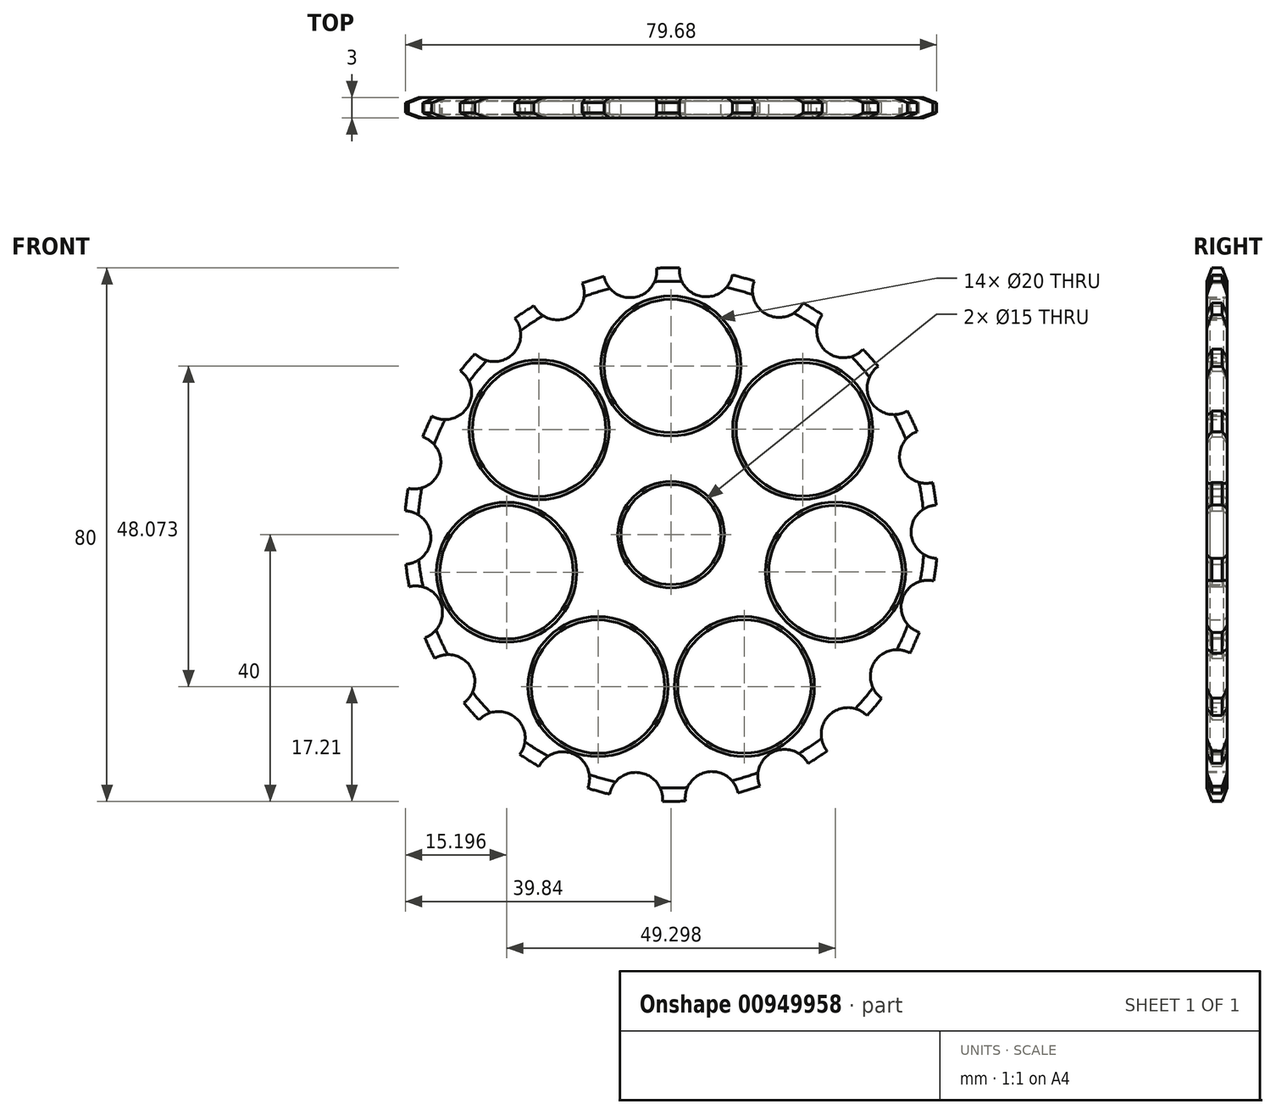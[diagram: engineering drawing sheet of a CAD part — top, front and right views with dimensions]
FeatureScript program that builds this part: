
annotation { "Feature Type Name" : "Feature", "Feature Type Description" : "" }
export const myFeature = defineFeature(function(context is Context, id is Id, definition is map)
    precondition{}
    {
        {
            var Q0;
            Q0=qCreatedBy(makeId("Front.planeOp"),FACE);
            var sketch = newSketch(context, id + "F0", { "sketchPlane" : qUnion([Q0])});
            skCircle(sketch, "E0", {"center": v(0, 0) * mm, "radius": 40 * mm});
            skCircle(sketch, "E1", {"center": v(-33.89, 21.25) * mm, "radius": 4 * mm});
            skCircle(sketch, "E2.1.0", {"center": v(-38.5, 10.85) * mm, "radius": 4 * mm});
            skCircle(sketch, "E2.2.0", {"center": v(-40, -0.44) * mm, "radius": 4 * mm});
            skCircle(sketch, "E2.3.0", {"center": v(-38.25, -11.7) * mm, "radius": 4 * mm});
            skCircle(sketch, "E2.4.0", {"center": v(-33.41, -22) * mm, "radius": 4 * mm});
            skCircle(sketch, "E2.5.0", {"center": v(-25.86, -30.52) * mm, "radius": 4 * mm});
            skCircle(sketch, "E2.6.0", {"center": v(-16.22, -36.57) * mm, "radius": 4 * mm});
            skCircle(sketch, "E2.7.0", {"center": v(-5.26, -39.65) * mm, "radius": 4 * mm});
            skCircle(sketch, "E2.8.0", {"center": v(6.13, -39.53) * mm, "radius": 4 * mm});
            skCircle(sketch, "E2.9.0", {"center": v(17.02, -36.2) * mm, "radius": 4 * mm});
            skCircle(sketch, "E2.10.0", {"center": v(26.53, -29.94) * mm, "radius": 4 * mm});
            skCircle(sketch, "E2.11.0", {"center": v(33.89, -21.25) * mm, "radius": 4 * mm});
            skCircle(sketch, "E2.12.0", {"center": v(38.5, -10.85) * mm, "radius": 4 * mm});
            skCircle(sketch, "E2.13.0", {"center": v(40, 0.44) * mm, "radius": 4 * mm});
            skCircle(sketch, "E2.14.0", {"center": v(38.25, 11.7) * mm, "radius": 4 * mm});
            skCircle(sketch, "E2.15.0", {"center": v(33.41, 22) * mm, "radius": 4 * mm});
            skCircle(sketch, "E2.16.0", {"center": v(25.86, 30.52) * mm, "radius": 4 * mm});
            skCircle(sketch, "E2.17.0", {"center": v(16.22, 36.57) * mm, "radius": 4 * mm});
            skCircle(sketch, "E2.18.0", {"center": v(5.26, 39.65) * mm, "radius": 4 * mm});
            skCircle(sketch, "E2.19.0", {"center": v(-6.13, 39.53) * mm, "radius": 4 * mm});
            skCircle(sketch, "E3", {"center": v(0, 0) * mm, "radius": 7.5 * mm});
            skCircle(sketch, "E4.1.20.0", {"center": v(-17.02, 36.2) * mm, "radius": 4 * mm});
            skCircle(sketch, "E4.1.21.0", {"center": v(-26.53, 29.94) * mm, "radius": 4 * mm});
            skCircle(sketch, "E5", {"center": v(-0.03, 25.28) * mm, "radius": 10 * mm});
            skCircle(sketch, "E6.1.0", {"center": v(-19.78, 15.74) * mm, "radius": 10 * mm});
            skCircle(sketch, "E6.2.0", {"center": v(-24.64, -5.65) * mm, "radius": 10 * mm});
            skCircle(sketch, "E6.3.0", {"center": v(-10.95, -22.8) * mm, "radius": 10 * mm});
            skCircle(sketch, "E6.4.0", {"center": v(11, -22.77) * mm, "radius": 10 * mm});
            skCircle(sketch, "E6.5.0", {"center": v(24.65, -5.6) * mm, "radius": 10 * mm});
            skCircle(sketch, "E6.6.0", {"center": v(19.75, 15.78) * mm, "radius": 10 * mm});
            skSolve(sketch);
        }
        {
            var Q0;
            Q0=makeQuery(id+"F0.imprint","IMPRINT",FACE,{"disambiguationData":[TD([[makeQuery(id+"F0.imprint","IMPRINT",EDGE,{"derivedFrom":sQuery(id+"F0.wireOp",EDGE,"E0")}),1.0]])]});
            extrude(context, id + "F1", {"entities" : qUnion([Q0]), "depth" : 3 * mm, "offsetDistance" : 25 * mm});
        }
        {
            var Q0;
            {var subQ0=sQuery(id+"F0.wireOp",EDGE,"E0");Q0=makeQuery(id+"FjPS6zSCau8WYdw_1.boolean.opBoolean","SPLIT",EDGE,{"disambiguationData":[TD([makeQuery(id+"F1.opExtrude","SWEPT_FACE",FACE,{"disambiguationData":[OSD([subQ0])]}),makeQuery(id+"F1.opExtrude","CAP_FACE",FACE,{"disambiguationData":[OSD([subQ0])],"isStart":false}),makeQuery(id+"FjPS6zSCau8WYdw_1.opExtrude","SWEPT_FACE",FACE,{"disambiguationData":[OSD([sQuery(id+"FptURnvkRjZK9U8_1.wireOp",EDGE,"c81c12ed-b287-469f-bd1e-95274906ad68.5.0")])]}),makeQuery(id+"FjPS6zSCau8WYdw_1.opExtrude","SWEPT_FACE",FACE,{"disambiguationData":[OSD([sQuery(id+"FptURnvkRjZK9U8_1.wireOp",EDGE,"c81c12ed-b287-469f-bd1e-95274906ad68.6.0")])]})])],"derivedFrom":makeQuery(id+"F1.opExtrude","CAP_EDGE",EDGE,{"disambiguationData":[OSD([subQ0])],"isStart":false})});}
            chamfer(context, id + "F2", {"entities" : qUnion([Q0]), "chamferType" : ChamferType.TWO_OFFSETS, "width1" : 2 * mm, "oppositeDirection" : false, "width2" : 0.75 * mm, "tangentPropagation" : true});
        }
        {
            var Q0;
            {var subQ0=sQuery(id+"F0.wireOp",EDGE,"E0");Q0=makeQuery(id+"FjPS6zSCau8WYdw_1.boolean.opBoolean","SPLIT",EDGE,{"disambiguationData":[TD([makeQuery(id+"F1.opExtrude","SWEPT_FACE",FACE,{"disambiguationData":[OSD([subQ0])]}),makeQuery(id+"F1.opExtrude","CAP_FACE",FACE,{"disambiguationData":[OSD([subQ0])],"isStart":true}),makeQuery(id+"FjPS6zSCau8WYdw_1.opExtrude","SWEPT_FACE",FACE,{"disambiguationData":[OSD([sQuery(id+"FptURnvkRjZK9U8_1.wireOp",EDGE,"c81c12ed-b287-469f-bd1e-95274906ad68.21.0")])]}),makeQuery(id+"FjPS6zSCau8WYdw_1.opExtrude","SWEPT_FACE",FACE,{"disambiguationData":[OSD([sQuery(id+"FptURnvkRjZK9U8_1.wireOp",EDGE,"c81c12ed-b287-469f-bd1e-95274906ad68.22.0")])]})])],"derivedFrom":makeQuery(id+"F1.opExtrude","CAP_EDGE",EDGE,{"disambiguationData":[OSD([subQ0])],"isStart":true})});}
            chamfer(context, id + "F3", {"entities" : qUnion([Q0]), "chamferType" : ChamferType.TWO_OFFSETS, "width1" : 0.75 * mm, "oppositeDirection" : false, "width2" : 2 * mm, "tangentPropagation" : true});
        }
        {
            var Q0;
            Q0=makeQuery(id+"F1.opExtrude","CAP_EDGE",EDGE,{"disambiguationData":[OSD([sQuery(id+"F0.wireOp",EDGE,"E3")])],"isStart":false});
            var Q1;
            Q1=makeQuery(id+"F1.opExtrude","CAP_EDGE",EDGE,{"disambiguationData":[OSD([sQuery(id+"F0.wireOp",EDGE,"E3")])],"isStart":true});
            var Q2;
            Q2=makeQuery(id+"F1.opExtrude","CAP_EDGE",EDGE,{"disambiguationData":[OSD([sQuery(id+"F0.wireOp",EDGE,"E5")])],"isStart":false});
            var Q3;
            Q3=makeQuery(id+"F1.opExtrude","CAP_EDGE",EDGE,{"disambiguationData":[OSD([sQuery(id+"F0.wireOp",EDGE,"E6.6.0")])],"isStart":false});
            var Q4;
            Q4=makeQuery(id+"F1.opExtrude","CAP_EDGE",EDGE,{"disambiguationData":[OSD([sQuery(id+"F0.wireOp",EDGE,"E6.5.0")])],"isStart":false});
            var Q5;
            Q5=makeQuery(id+"F1.opExtrude","CAP_EDGE",EDGE,{"disambiguationData":[OSD([sQuery(id+"F0.wireOp",EDGE,"E6.4.0")])],"isStart":false});
            var Q6;
            Q6=makeQuery(id+"F1.opExtrude","CAP_EDGE",EDGE,{"disambiguationData":[OSD([sQuery(id+"F0.wireOp",EDGE,"E6.3.0")])],"isStart":false});
            var Q7;
            Q7=makeQuery(id+"F1.opExtrude","CAP_EDGE",EDGE,{"disambiguationData":[OSD([sQuery(id+"F0.wireOp",EDGE,"E6.2.0")])],"isStart":false});
            var Q8;
            Q8=makeQuery(id+"F1.opExtrude","CAP_EDGE",EDGE,{"disambiguationData":[OSD([sQuery(id+"F0.wireOp",EDGE,"E6.1.0")])],"isStart":false});
            var Q9;
            Q9=makeQuery(id+"F1.opExtrude","CAP_EDGE",EDGE,{"disambiguationData":[OSD([sQuery(id+"F0.wireOp",EDGE,"E5")])],"isStart":true});
            var Q10;
            Q10=makeQuery(id+"F1.opExtrude","CAP_EDGE",EDGE,{"disambiguationData":[OSD([sQuery(id+"F0.wireOp",EDGE,"E6.6.0")])],"isStart":true});
            var Q11;
            Q11=makeQuery(id+"F1.opExtrude","CAP_EDGE",EDGE,{"disambiguationData":[OSD([sQuery(id+"F0.wireOp",EDGE,"E6.5.0")])],"isStart":true});
            var Q12;
            Q12=makeQuery(id+"F1.opExtrude","CAP_EDGE",EDGE,{"disambiguationData":[OSD([sQuery(id+"F0.wireOp",EDGE,"E6.4.0")])],"isStart":true});
            var Q13;
            Q13=makeQuery(id+"F1.opExtrude","CAP_EDGE",EDGE,{"disambiguationData":[OSD([sQuery(id+"F0.wireOp",EDGE,"E6.3.0")])],"isStart":true});
            var Q14;
            Q14=makeQuery(id+"F1.opExtrude","CAP_EDGE",EDGE,{"disambiguationData":[OSD([sQuery(id+"F0.wireOp",EDGE,"E6.2.0")])],"isStart":true});
            var Q15;
            Q15=makeQuery(id+"F1.opExtrude","CAP_EDGE",EDGE,{"disambiguationData":[OSD([sQuery(id+"F0.wireOp",EDGE,"E6.1.0")])],"isStart":true});
            chamfer(context, id + "F4", {"entities" : qUnion([Q0, Q1, Q2, Q3, Q4, Q5, Q6, Q7, Q8, Q9, Q10, Q11, Q12, Q13, Q14, Q15]), "width" : 0.5 * mm, "tangentPropagation" : true});
        }
    });
